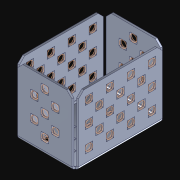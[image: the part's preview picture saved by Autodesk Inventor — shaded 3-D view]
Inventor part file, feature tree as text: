
AUTODESK INVENTOR PART (.ipt)
format: ipt  version: 2021.3 (Build 253353010, 353A)  size: 921,600 bytes
history: native  units: in
note: dims shown in document units (in); Inventor stores cm internally (conversion verified against a paired STEP export)
features: other x62, extrude x61, pattern_linear x10, sketch x5, imported_body x1
ambient origin geometry x8: Origin, YZ Plane, XZ Plane, XY Plane, X Axis, Y Axis, Z Axis, Center Point
bodies: Body1 (feature_tree), Body2 (feature_tree), Body3 (feature_tree), Body4 (feature_tree), Body5 (feature_tree), Body6 (feature_tree), Body7 (feature_tree), Body8 (feature_tree), Body9 (feature_tree), Body10 (feature_tree), Body11 (feature_tree), Body12 (feature_tree), Body13 (feature_tree), Body14 (feature_tree), Body15 (feature_tree), Body16 (feature_tree), Body17 (feature_tree), Body18 (feature_tree), Body19 (feature_tree), Body20 (feature_tree), Body21 (feature_tree), Body22 (feature_tree), Body23 (feature_tree), Body24 (feature_tree), Body25 (feature_tree), Body26 (feature_tree), Body27 (feature_tree), Body28 (feature_tree), Body29 (feature_tree), Body30 (feature_tree), Body31 (feature_tree), Body32 (feature_tree), Body33 (feature_tree), Body34 (feature_tree), Body35 (feature_tree), Body36 (feature_tree), Body37 (feature_tree), Body38 (feature_tree), Body39 (feature_tree), Body40 (feature_tree), Body41 (feature_tree), Body42 (feature_tree), Body43 (feature_tree), Body44 (feature_tree), Body45 (feature_tree), Body46 (feature_tree), Body47 (feature_tree), Body48 (feature_tree), Body49 (feature_tree), Body50 (feature_tree), Body51 (feature_tree), Body52 (feature_tree), Body53 (feature_tree), Body54 (feature_tree), Body55 (feature_tree), Body56 (feature_tree), Body57 (feature_tree), Body58 (feature_tree), Body59 (feature_tree), Body60 (feature_tree), Body61 (feature_tree), Body62 (feature_tree)
feature tree (139):
  parser-record x1  (decoder bookkeeping rows leaked as tree rows — omitted from the tree; the rows remain in map.json)
  imported_body  "Base1"
  pattern_linear  "Rectangular Pattern1"  Count1=3 Spacing1=0.5in
  pattern_linear  "Rectangular Pattern2"  Count1=2 Spacing1=0.5in
  pattern_linear  "Rectangular Pattern3"  Count1=2 Spacing1=0.5in
  pattern_linear  "Rectangular Pattern4"  Count1=4 Spacing1=0.5in
  pattern_linear  "Rectangular Pattern5"  Count1=3 Spacing1=0.5in
  pattern_linear  "Rectangular Pattern6"  Count1=3 Spacing1=0.5in
  pattern_linear  "Rectangular Pattern7"  Count1=2 Spacing1=0.5in
  pattern_linear  "Rectangular Pattern8"  Count1=4 Spacing1=0.5in
  pattern_linear  "Rectangular Pattern9"  Count1=3 Spacing1=0.5in
  pattern_linear  "Rectangular Pattern10"  Spacing1=0.046in  [1 undecoded]
  other  "Srf1"
  other  "Srf2"
  other  "Srf3"
  other  "Srf4"
  other  "Srf5"
  other  "Srf6"
  other  "Srf7"
  other  "Srf8"
  other  "Srf9"
  other  "Srf10"
  other  "Srf11"
  other  "Srf12"
  other  "Srf13"
  other  "Srf14"
  other  "Srf15"
  other  "Srf16"
  other  "Srf17"
  other  "Srf18"
  other  "Srf19"
  other  "Srf20"
  other  "Srf21"
  other  "Srf22"
  other  "Srf23"
  other  "Srf24"
  other  "Srf25"
  other  "Srf26"
  other  "Srf27"
  other  "Srf28"
  other  "Srf29"
  other  "Srf30"
  other  "Srf31"
  other  "Srf32"
  other  "Srf33"
  other  "Srf34"
  other  "Srf35"
  other  "Srf36"
  other  "Srf37"
  sketch  "Sketch6"  dims[d70=0.046in d71=0.0in d72=1.1811in d74=0.5in]
  other  "Srf38"
  other  "Srf39"
  other  "Srf40"
  other  "Srf41"
  other  "Srf42"
  other  "Srf43"
  sketch  "Sketch7"  dims[d76=0.046in d77=0.0in d78=0.7874in d80=0.5in d81=0.7874in d83=0.5in]
  other  "Srf44"
  other  "Srf45"
  other  "Srf46"
  sketch  "Sketch8"  dims[d85=0.046in d86=0.0in d87=1.5748in d89=0.5in d90=1.1811in d92=0.5in]
  other  "Srf47"
  other  "Srf48"
  other  "Srf49"
  other  "Srf50"
  sketch  "Sketch9"  dims[d94=0.046in d95=0.0in d96=1.1811in d98=0.5in d99=0.7874in d101=0.5in]
  other  "Srf51"
  other  "Srf52"
  other  "Srf53"
  other  "Srf54"
  other  "Srf55"
  other  "Srf56"
  other  "Srf57"
  other  "Srf58"
  sketch  "Sketch10"  dims[d103=0.046in d104=0.0in d105=1.5748in d107=0.5in d108=1.1811in d110=0.5in d112=0.046in d113=0.0in d114=1.1811in d116=0.5in d117=0.7874in d119=0.5in d121=0.046in d122=0.0in d123=1.1811in d125=0.5in d127=0.046in d128=0.0in d129=0.7874in d131=0.5in d132=0.7874in d134=0.5in d136=0.046in d137=0.0in d138=1.5748in d140=0.5in d141=0.7874in d143=0.5in d145=0.046in d146=0.0in d147=1.1811in d149=0.5in d150=0.0in d151=0.0in d152=0.0in d153=0.0in d154=0.0in d155=0.0in d156=0.0in d157=0.0in d158=0.0in d159=0.0in d160=0.0in d161=0.0in d162=0.0in d163=0.0in d164=0.0in d165=0.0in d166=0.0in d167=0.0in d168=0.0in d169=0.0in d170=0.0in d171=0.0in d172=0.0in d173=0.0in d174=0.0in d175=0.0in d176=0.0in d177=0.0in d178=0.0in d179=0.0in d180=0.0in d181=0.0in d182=0.0in d183=0.0in d184=0.0in d185=0.0in d186=0.0in d187=0.0in d188=0.0in d189=0.0in d190=0.0in d191=0.0in d192=0.0in d193=0.0in d194=0.0in d195=0.0in d196=0.0in d197=0.0in d198=0.0in d199=0.0in d200=0.0in d201=0.0in d202=0.0in d203=0.0in d204=0.0in d205=0.0in d206=0.0in d207=0.0in d208=0.0in d209=0.0in d210=0.0in d211=0.0in d212=0.0in d213=0.0in d214=0.0in d215=0.0in d216=0.0in d217=0.0in d218=0.0in d219=0.0in d220=0.0in d221=0.0in d222=0.0in d223=0.0in d224=0.0in d225=0.0in d226=0.0in d227=0.0in d228=0.0in d229=0.0in d230=0.0in d231=0.0in d232=0.0in d233=0.0in d234=0.0in d235=0.0in d236=0.0in d237=0.0in d238=0.0in d239=0.0in d240=0.0in d241=0.0in d242=0.0in d243=0.0in d244=0.0in d245=0.0in d246=0.0in d247=0.0in d248=0.0in d249=0.0in d250=0.0in d251=0.0in d252=0.0in d253=0.0in d254=0.0in d255=0.0in d256=0.0in d257=0.0in d258=0.0in d259=0.0in d260=0.0in d261=0.0in d262=0.0in d263=0.0in d264=0.0in d265=0.0in d266=0.0in d267=0.0in d268=0.0in d269=0.0in d270=0.0in d271=0.0in]
  other  "Srf59"
  other  "Srf60"
  other  "Srf61"
  extrude  "ExtrusionSrf1"  Depth=0.5in
  extrude  "ExtrusionSrf4"  Depth=0.5in
  extrude  "ExtrusionSrf8"  Depth=0.046in TaperAngle=0.0deg
  extrude  "ExtrusionSrf20"  Depth=0.5in
  extrude  "ExtrusionSrf26"  Depth=0.046in TaperAngle=0.0deg
  extrude  "ExtrusionSrf38"  Depth=0.5in
  extrude  "ExtrusionSrf44"  Depth=0.5in
  extrude  "ExtrusionSrf47"  Depth=0.046in TaperAngle=0.0deg
  extrude  "ExtrusionSrf51"  Depth=0.5in
  extrude  "ExtrusionSrf59"  Depth=0.5in
  extrude  "ExtrusionSrf2"  Depth=0.046in TaperAngle=0.0deg
  extrude  "ExtrusionSrf3"  Depth=0.5in
  extrude  "ExtrusionSrf5"  TaperAngle=0.0deg  [1 undecoded]
  extrude  "ExtrusionSrf6"  TaperAngle=0.0deg  [1 undecoded]
  extrude  "ExtrusionSrf7"  TaperAngle=0.0deg  [1 undecoded]
  extrude  "ExtrusionSrf9"  TaperAngle=0.0deg  [1 undecoded]
  extrude  "ExtrusionSrf10"  TaperAngle=0.0deg  [1 undecoded]
  extrude  "ExtrusionSrf11"  TaperAngle=0.0deg  [1 undecoded]
  extrude  "ExtrusionSrf12"  TaperAngle=0.0deg  [1 undecoded]
  extrude  "ExtrusionSrf13"  TaperAngle=0.0deg  [1 undecoded]
  extrude  "ExtrusionSrf14"  TaperAngle=0.0deg  [1 undecoded]
  extrude  "ExtrusionSrf15"  TaperAngle=0.0deg  [1 undecoded]
  extrude  "ExtrusionSrf16"  TaperAngle=0.0deg  [1 undecoded]
  extrude  "ExtrusionSrf17"  TaperAngle=0.0deg  [1 undecoded]
  extrude  "ExtrusionSrf18"  TaperAngle=0.0deg  [1 undecoded]
  extrude  "ExtrusionSrf19"  TaperAngle=0.0deg  [1 undecoded]
  extrude  "ExtrusionSrf21"  TaperAngle=0.0deg  [1 undecoded]
  extrude  "ExtrusionSrf22"  TaperAngle=0.0deg  [1 undecoded]
  extrude  "ExtrusionSrf23"  TaperAngle=0.0deg  [1 undecoded]
  extrude  "ExtrusionSrf24"  TaperAngle=0.0deg  [1 undecoded]
  extrude  "ExtrusionSrf25"  TaperAngle=0.0deg  [1 undecoded]
  extrude  "ExtrusionSrf27"  TaperAngle=0.0deg  [1 undecoded]
  extrude  "ExtrusionSrf28"  TaperAngle=0.0deg  [1 undecoded]
  extrude  "ExtrusionSrf29"  TaperAngle=0.0deg  [1 undecoded]
  extrude  "ExtrusionSrf30"  TaperAngle=0.0deg  [1 undecoded]
  extrude  "ExtrusionSrf31"  TaperAngle=0.0deg  [1 undecoded]
  extrude  "ExtrusionSrf32"  TaperAngle=0.0deg  [1 undecoded]
  extrude  "ExtrusionSrf33"  TaperAngle=0.0deg  [1 undecoded]
  extrude  "ExtrusionSrf34"  TaperAngle=0.0deg  [1 undecoded]
  extrude  "ExtrusionSrf35"  TaperAngle=0.0deg  [1 undecoded]
  extrude  "ExtrusionSrf36"  TaperAngle=0.0deg  [1 undecoded]
  extrude  "ExtrusionSrf37"  TaperAngle=0.0deg  [1 undecoded]
  extrude  "ExtrusionSrf39"  TaperAngle=0.0deg  [1 undecoded]
  extrude  "ExtrusionSrf40"  TaperAngle=0.0deg  [1 undecoded]
  extrude  "ExtrusionSrf41"  TaperAngle=0.0deg  [1 undecoded]
  extrude  "ExtrusionSrf42"  TaperAngle=0.0deg  [1 undecoded]
  extrude  "ExtrusionSrf43"  TaperAngle=0.0deg  [1 undecoded]
  extrude  "ExtrusionSrf45"  TaperAngle=0.0deg  [1 undecoded]
  extrude  "ExtrusionSrf46"  TaperAngle=0.0deg  [1 undecoded]
  extrude  "ExtrusionSrf48"  TaperAngle=0.0deg  [1 undecoded]
  extrude  "ExtrusionSrf49"  TaperAngle=0.0deg  [1 undecoded]
  extrude  "ExtrusionSrf50"  TaperAngle=0.0deg  [1 undecoded]
  extrude  "ExtrusionSrf52"  TaperAngle=0.0deg  [1 undecoded]
  extrude  "ExtrusionSrf53"  TaperAngle=0.0deg  [1 undecoded]
  extrude  "ExtrusionSrf54"  TaperAngle=0.0deg  [1 undecoded]
  extrude  "ExtrusionSrf55"  TaperAngle=0.0deg  [1 undecoded]
  extrude  "ExtrusionSrf56"  TaperAngle=0.0deg  [1 undecoded]
  extrude  "ExtrusionSrf57"  TaperAngle=0.0deg  [1 undecoded]
  extrude  "ExtrusionSrf58"  TaperAngle=0.0deg  [1 undecoded]
  extrude  "ExtrusionSrf60"  TaperAngle=0.0deg  [1 undecoded]
  extrude  "ExtrusionSrf61"  TaperAngle=0.0deg  [1 undecoded]
note: 50 required parameter values undecoded (feature->parameter linkage not recoverable at this tier; creation-order binding heuristic only, values carry confidence <= 0.55)
